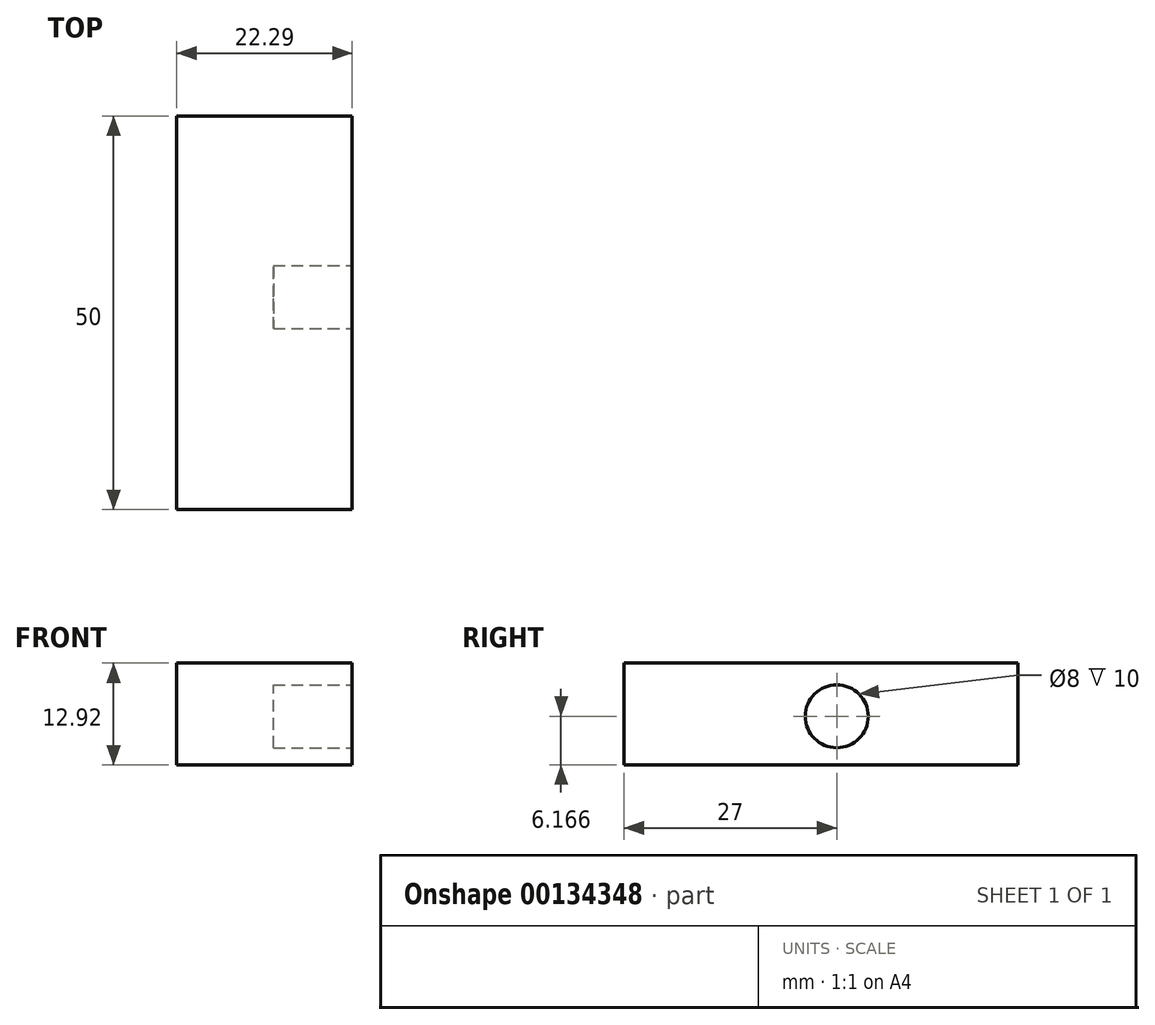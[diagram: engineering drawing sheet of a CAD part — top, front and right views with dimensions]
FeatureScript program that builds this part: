
annotation { "Feature Type Name" : "Feature", "Feature Type Description" : "" }
export const myFeature = defineFeature(function(context is Context, id is Id, definition is map)
    precondition{}
    {
        {
            var Q0;
            Q0=qCreatedBy(makeId("Front.planeOp"),FACE);
            var sketch = newSketch(context, id + "F0", { "sketchPlane" : qUnion([Q0])});
            skLineSegment(sketch, "E0.bottom", {"start": v(25.02, -27.66) * mm, "end": v(-24.98, -27.66) * mm});
            skLineSegment(sketch, "E0.top", {"start": v(25.02, 22.34) * mm, "end": v(-24.98, 22.34) * mm});
            skLineSegment(sketch, "E0.left", {"start": v(25.02, -27.66) * mm, "end": v(25.02, 22.34) * mm});
            skLineSegment(sketch, "E0.right", {"start": v(-24.98, -27.66) * mm, "end": v(-24.98, 22.34) * mm});
            skPoint(sketch, "E0.middle", {"position": v(0.02, -2.66) * mm});
            skLineSegment(sketch, "E1", {"start": v(11.1, 22.34) * mm, "end": v(11.1, 9.42) * mm});
            skLineSegment(sketch, "E2", {"start": v(11.1, 9.42) * mm, "end": v(-11.19, 9.42) * mm});
            skLineSegment(sketch, "E3", {"start": v(-11.19, 9.42) * mm, "end": v(-11.19, 22.34) * mm});
            skLineSegment(sketch, "E4", {"start": v(25.02, -9.38) * mm, "end": v(0.02, -9.38) * mm});
            skLineSegment(sketch, "E5", {"start": v(0.02, -9.38) * mm, "end": v(0.02, 9.42) * mm});
            skLineSegment(sketch, "E6", {"start": v(0.02, -9.38) * mm, "end": v(-24.98, -27.66) * mm});
            skSolve(sketch);
        }
        {
            var Q0;
            {var subQ3=sQuery(id+"F0.wireOp",EDGE,"E1");Q0=makeQuery(id+"F0.imprint","IMPRINT",FACE,{"disambiguationData":[TD([[makeQuery(id+"F0.imprint","IMPRINT",EDGE,{"derivedFrom":subQ3}),-1.0]])]});}
            extrude(context, id + "F1", {"entities" : qUnion([Q0]), "depth" : 50 * mm});
        }
        {
            var Q0;
            Q0=makeQuery(id+"F1.opExtrude","SWEPT_FACE",FACE,{"disambiguationData":[OSD([sQuery(id+"F0.wireOp",EDGE,"E1")])]});
            var sketch = newSketch(context, id + "F2", { "sketchPlane" : qUnion([Q0])});
            skCircle(sketch, "E7", {"center": v(-23, 15.59) * mm, "radius": 4 * mm});
            skSolve(sketch);
        }
        {
            var Q0;
            Q0=makeQuery(id+"F2.imprint","IMPRINT",FACE,{"disambiguationData":[TD([[makeQuery(id+"F2.imprint","IMPRINT",EDGE,{"derivedFrom":sQuery(id+"F2.wireOp",EDGE,"E7")}),1.0]])]});
            extrude(context, id + "F3", {"entities" : qUnion([Q0]), "operationType" : NewBodyOperationType.REMOVE, "oppositeDirection" : true, "depth" : 10 * mm});
        }
    });
